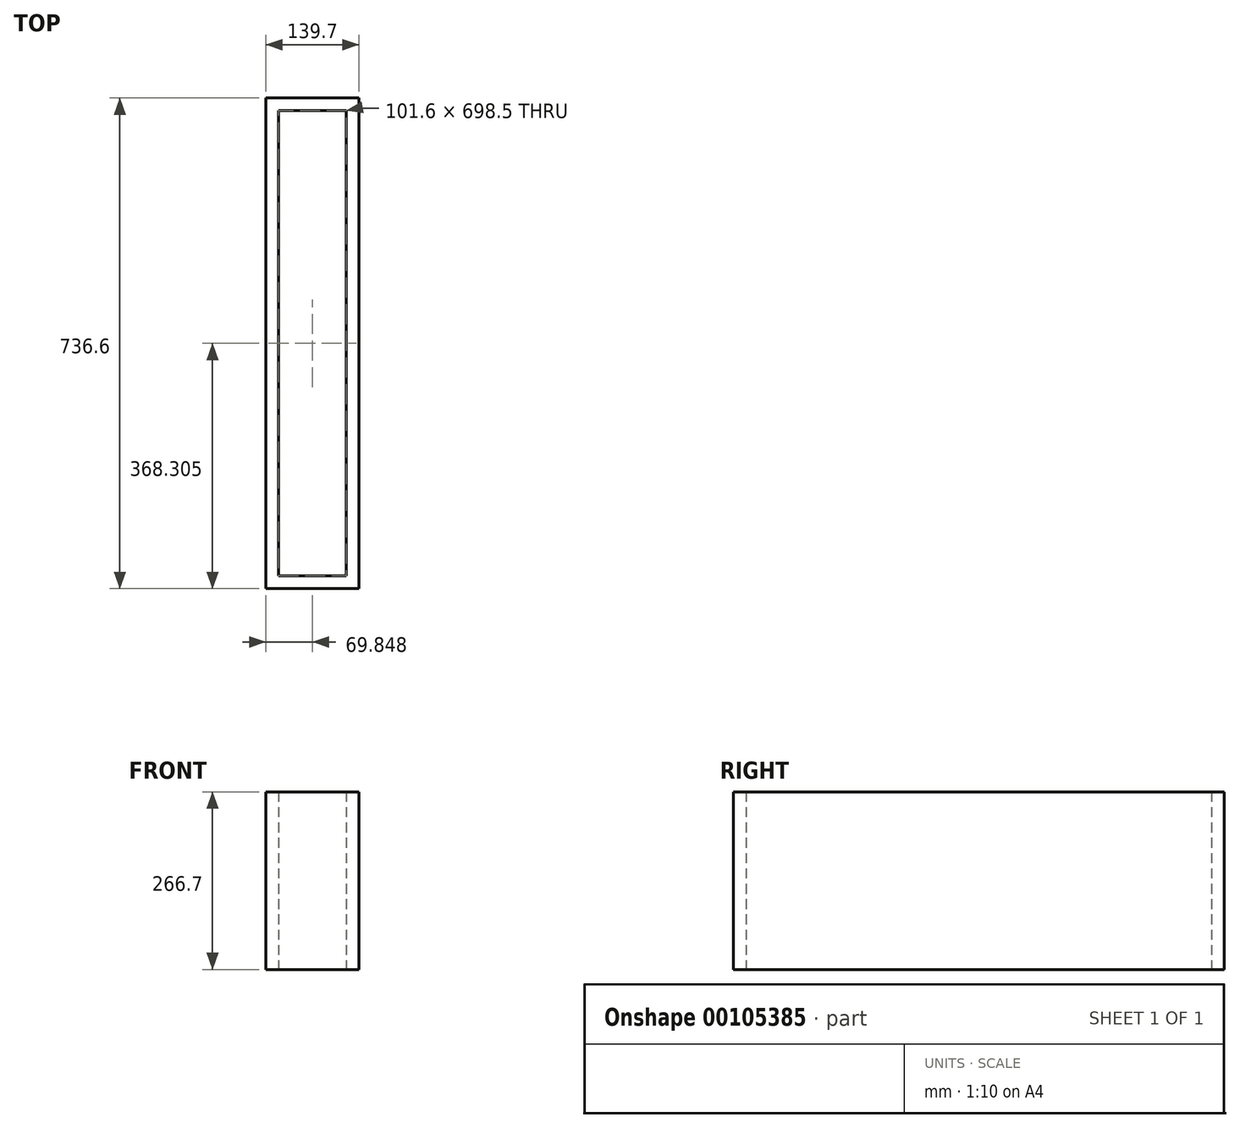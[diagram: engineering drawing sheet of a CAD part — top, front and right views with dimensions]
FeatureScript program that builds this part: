
annotation { "Feature Type Name" : "Feature", "Feature Type Description" : "" }
export const myFeature = defineFeature(function(context is Context, id is Id, definition is map)
    precondition{}
    {
        {
            var Q0;
            Q0=qCreatedBy(makeId("Top.planeOp"),FACE);
            var sketch = newSketch(context, id + "F0", { "sketchPlane" : qUnion([Q0])});
            skLineSegment(sketch, "E0.bottom", {"start": v(-101.8, 577.54) * mm, "end": v(37.9, 577.54) * mm});
            skLineSegment(sketch, "E0.top", {"start": v(-101.8, -159.06) * mm, "end": v(37.9, -159.06) * mm});
            skLineSegment(sketch, "E0.left", {"start": v(-101.8, 577.54) * mm, "end": v(-101.8, -159.06) * mm});
            skLineSegment(sketch, "E0.right", {"start": v(37.9, 577.54) * mm, "end": v(37.9, -159.06) * mm});
            skSolve(sketch);
        }
        {
            var Q0;
            Q0 = qSketchRegion(id + "F0", true);
            extrude(context, id + "F1", {"entities" : qUnion([Q0]), "depth" : 266.7 * mm});
        }
        {
            var Q0;
            Q0=makeQuery(id+"F1.opExtrude","CAP_FACE",FACE,{"disambiguationData":[OSD([sQuery(id+"F0.wireOp",EDGE,"E0.bottom"),sQuery(id+"F0.wireOp",EDGE,"E0.top"),sQuery(id+"F0.wireOp",EDGE,"E0.left"),sQuery(id+"F0.wireOp",EDGE,"E0.right")])],"isStart":false});
            var Q1;
            Q1=makeQuery(id+"F1.opExtrude","CAP_FACE",FACE,{"disambiguationData":[OSD([sQuery(id+"F0.wireOp",EDGE,"E0.bottom"),sQuery(id+"F0.wireOp",EDGE,"E0.top"),sQuery(id+"F0.wireOp",EDGE,"E0.left"),sQuery(id+"F0.wireOp",EDGE,"E0.right")])],"isStart":true});
            shell(context, id + "F2", {"entities" : qUnion([Q0, Q1]), "thickness" : 19.05 * mm});
        }
    });
